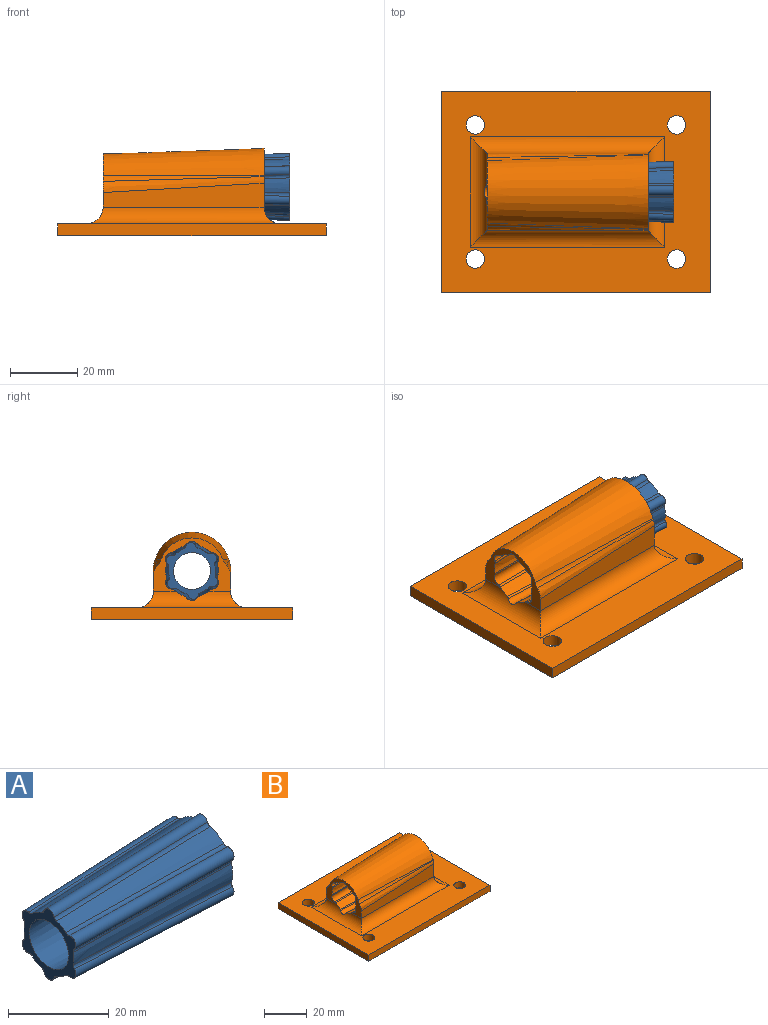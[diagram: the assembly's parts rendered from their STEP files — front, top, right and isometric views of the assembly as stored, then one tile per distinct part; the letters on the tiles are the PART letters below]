
ASSEMBLY  parts=2 mates=1
PART A: 27 faces, bbox 59.1x18.4x20.1 mm
  f0: cone r=7mm half-angle=2deg, axis (1,0,0), area 161.8mm2, adj f5,f7,f11,f25
  f1: cone r=7mm half-angle=2deg, axis (1,0,0), area 161.8mm2, adj f5,f7,f22,f26
  f2: cone r=7mm half-angle=2deg, axis (1,0,0), area 161.8mm2, adj f5,f7,f19,f23
  f3: cone r=7mm half-angle=2deg, axis (1,0,0), area 161.8mm2, adj f5,f7,f16,f20
  f4: cone r=7mm half-angle=2deg, axis (1,0,0), area 161.8mm2, adj f5,f7,f13,f17
  f5: plane 20.08x17.81mm, normal (1,0,0), area 96mm2, adj f0,f1,f2,f3,f4,f6,f8,f9
  f6: cone r=7mm half-angle=2deg, axis (1,0,0), area 161.8mm2, adj f5,f7,f10,f14
  f7: plane 17.08x15.21mm, normal (-1,0,0), area 81.9mm2, adj f0,f1,f2,f3,f4,f6,f8,f9
  f8: cone r=5.5mm half-angle=2deg, axis (1,0,0), area 1687.8mm2, adj f5,f7
  f9: bspline ~42.95x3.27mm, area 168.2mm2, adj f5,f7,f10,f11
  f10: bspline ~55.78x2.7mm, area 44mm2, adj f5,f6,f7,f9
  f11: bspline ~55.78x2.7mm, area 44mm2, adj f0,f5,f7,f9
  f12: bspline ~42.95x4.04mm, area 168.2mm2, adj f5,f7,f13,f14
  f13: bspline ~55.78x2.12mm, area 44mm2, adj f4,f5,f7,f12
  f14: bspline ~55.78x2.68mm, area 44mm2, adj f5,f6,f7,f12
  f15: bspline ~42.95x4.04mm, area 168.2mm2, adj f5,f7,f16,f17
  f16: bspline ~55.78x2.68mm, area 44mm2, adj f3,f5,f7,f15
  f17: bspline ~55.78x2.12mm, area 44mm2, adj f4,f5,f7,f15
  f18: bspline ~42.95x3.27mm, area 168.2mm2, adj f5,f7,f19,f20
  f19: bspline ~55.78x2.7mm, area 44mm2, adj f2,f5,f7,f18
  f20: bspline ~55.78x2.7mm, area 44mm2, adj f3,f5,f7,f18
  f21: bspline ~42.95x4.04mm, area 168.2mm2, adj f5,f7,f22,f23
  f22: bspline ~55.78x2.12mm, area 44mm2, adj f1,f5,f7,f21
  f23: bspline ~55.78x2.68mm, area 44mm2, adj f2,f5,f7,f21
  f24: bspline ~42.95x4.04mm, area 168.2mm2, adj f5,f7,f25,f26
  f25: bspline ~55.78x2.68mm, area 44mm2, adj f0,f5,f7,f24
  f26: bspline ~55.78x2.12mm, area 44mm2, adj f1,f5,f7,f24
PART B: 47 faces, bbox 115.4x60.2x26.2 mm
  f0: plane 23.16x17.66mm, normal (1,0,0), area 85.4mm2, adj f2,f3,f4,f7,f8,f9,f10,f11
  f1: plane 23.13x15.96mm, normal (-1,0,0), area 99.8mm2, adj f2,f3,f4,f5,f6,f7,f8,f9
  f2: plane 47.99x7.13mm, normal (0,1,0), area 267mm2, adj f0,f1,f14,f46
  f3: plane 47.99x7.13mm, normal (0,-1,0), area 267mm2, adj f0,f1,f13,f43
  f4: cone r=9.5mm half-angle=2deg, axis (1,0,0), area 217.4mm2, adj f0,f1,f29,f31
  f5: cone r=9.5mm half-angle=2deg, axis (1,0,0), area 221.1mm2, adj f1,f26,f28,f44,f45
  f6: cone r=9.5mm half-angle=2deg, axis (1,0,0), area 221.1mm2, adj f1,f23,f25,f44,f45
  f7: cone r=9.5mm half-angle=2deg, axis (1,0,0), area 217.4mm2, adj f0,f1,f20,f22
  f8: cone r=9.5mm half-angle=2deg, axis (1,0,0), area 217.4mm2, adj f0,f1,f17,f19
  f9: cone r=9.82mm half-angle=2deg, axis (1,0,0), area 1275.1mm2, adj f0,f1,f11,f12
  f10: cone r=9.5mm half-angle=2deg, axis (1,0,0), area 217.4mm2, adj f0,f1,f16,f32
  f11: bspline ~82.73x7.73mm, area 56.8mm2, adj f0,f1,f9,f14
  f12: bspline ~93.22x8.09mm, area 56.8mm2, adj f0,f1,f9,f13
  f13: bspline ~59.88x5.21mm, area 138.8mm2, adj f0,f1,f3,f12
  f14: bspline ~53.36x4.96mm, area 138.9mm2, adj f0,f1,f2,f11
  f15: bspline ~47.99x4.18mm, area 188.2mm2, adj f0,f1,f16,f17
  f16: bspline ~65.22x2.76mm, area 34.5mm2, adj f0,f1,f10,f15
  f17: bspline ~65.22x2.76mm, area 34.5mm2, adj f0,f1,f8,f15
  f18: bspline ~47.99x5.23mm, area 188.2mm2, adj f0,f1,f19,f20
  f19: bspline ~63.98x2.64mm, area 34.5mm2, adj f0,f1,f8,f18
  f20: bspline ~65.14x2.17mm, area 34.5mm2, adj f0,f1,f7,f18
  f21: bspline ~48.47x5.24mm, area 188.2mm2, adj f0,f1,f22,f23,f45
  f22: bspline ~63.96x2.13mm, area 34.5mm2, adj f0,f1,f7,f21
  f23: bspline ~65.13x2.68mm, area 34.5mm2, adj f1,f6,f21,f45
  f24: bspline ~52.53x4.33mm, area 196mm2, adj f25,f26,f44,f45
  f25: bspline ~63.97x2.71mm, area 35.7mm2, adj f6,f24,f44,f45
  f26: bspline ~64.79x2.75mm, area 35.7mm2, adj f5,f24,f44,f45
  f27: bspline ~48.47x5.24mm, area 188.2mm2, adj f0,f1,f28,f29,f45
  f28: bspline ~63.98x2.64mm, area 34.5mm2, adj f1,f5,f27,f45
  f29: bspline ~64.37x2.15mm, area 34.5mm2, adj f0,f1,f4,f27
  f30: bspline ~47.99x5.23mm, area 188.2mm2, adj f0,f1,f31,f32
  f31: bspline ~63.96x2.13mm, area 34.5mm2, adj f0,f1,f4,f30
  f32: bspline ~63.98x2.65mm, area 34.5mm2, adj f0,f1,f10,f30
  f33: plane 80x60mm, normal (0,0,1), area 2791.3mm2, adj f34,f35,f36,f37,f38,f39,f40,f41
  f34: plane 80x3.5mm, normal (0,1,0), area 280mm2, adj f33,f35,f41,f42
  f35: plane 60x3.5mm, normal (1,0,0), area 210mm2, adj f33,f34,f36,f42
  f36: plane 80x3.5mm, normal (0,-1,0), area 280mm2, adj f33,f35,f41,f42
  f37: cylinder r=2.75mm len=5.5mm, axis (0,0,1), area 60.5mm2, adj f33,f42
  f38: cylinder r=2.75mm len=5.5mm, axis (0,0,1), area 60.5mm2, adj f33,f42
  f39: cylinder r=2.75mm len=5.5mm, axis (0,0,1), area 60.5mm2, adj f33,f42
  f40: cylinder r=2.75mm len=5.5mm, axis (0,0,1), area 60.5mm2, adj f33,f42
  f41: plane 60x3.5mm, normal (-1,0,0), area 210mm2, adj f33,f34,f36,f42
  f42: plane 80x60mm, normal (0,0,-1), area 4705mm2, adj f34,f35,f36,f37,f38,f39,f40,f41
  f43: cylinder r=5mm len=57.99mm, axis (1,0,0), area 416.2mm2, adj f3,f33,f44,f45
  f44: cylinder r=5mm len=33mm, axis (0,-1,0), area 194.1mm2, adj f1,f5,f6,f24,f25,f26,f33,f43
  f45: cylinder r=5mm len=33mm, axis (0,1,0), area 167.4mm2, adj f0,f5,f6,f21,f23,f24,f25,f26
  f46: cylinder r=5mm len=57.99mm, axis (-1,0,0), area 416.2mm2, adj f2,f33,f44,f45
PLACE A rot(axis=(-1,0,0),63deg) t=(3.78,1.16,12.89)mm
PLACE B t=(-3.9,1.16,12.89)mm fixed
MATE cylindrical A.f0 <-> B.f4  axis (1,0,0) through (3.78,1.16,12.89)mm
